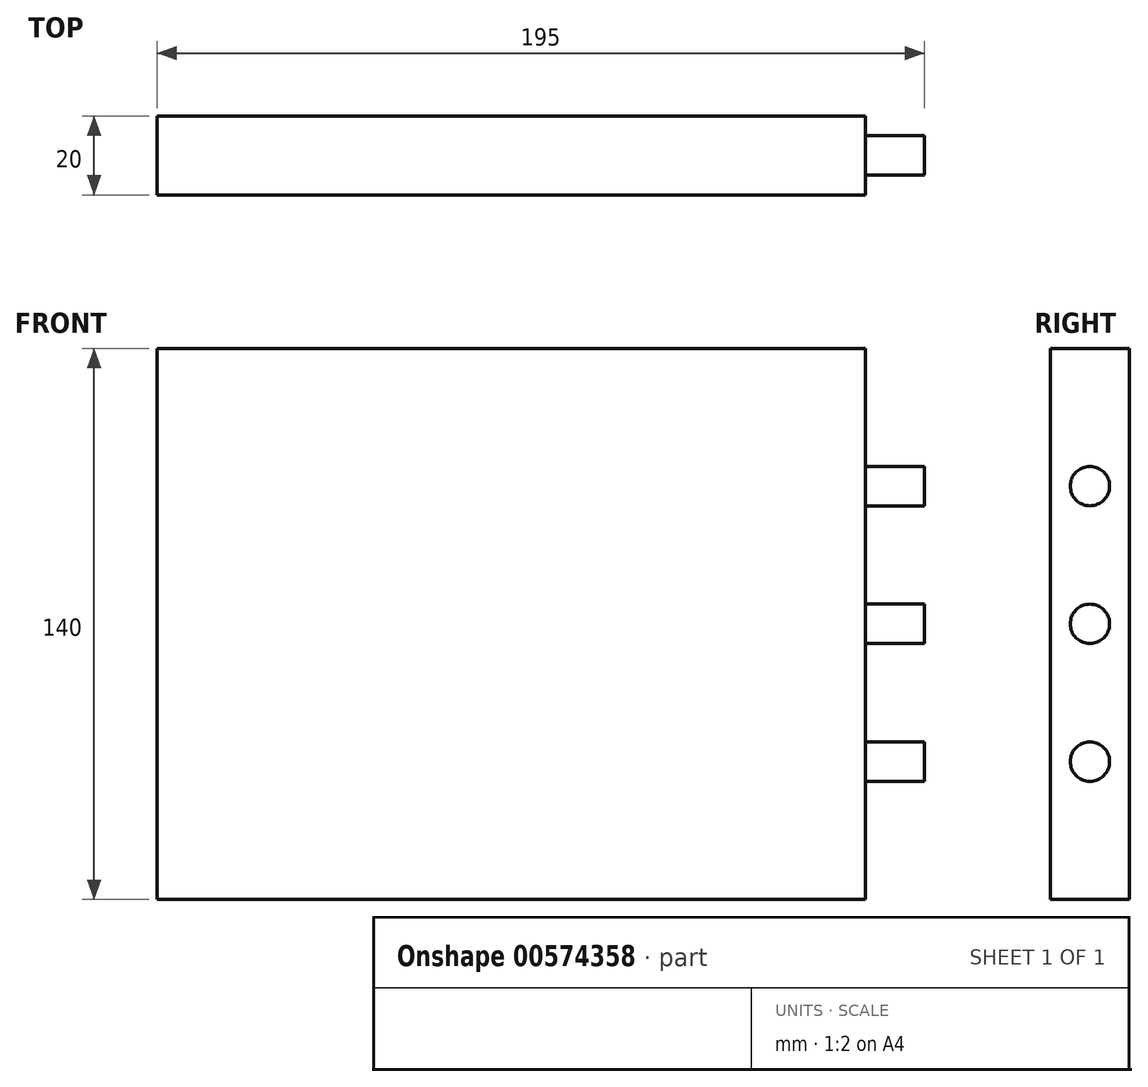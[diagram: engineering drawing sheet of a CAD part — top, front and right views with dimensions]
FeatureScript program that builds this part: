
annotation { "Feature Type Name" : "Feature", "Feature Type Description" : "" }
export const myFeature = defineFeature(function(context is Context, id is Id, definition is map)
    precondition{}
    {
        {
            var Q0;
            Q0=qCreatedBy(makeId("Front.planeOp"),FACE);
            var sketch = newSketch(context, id + "F0", { "sketchPlane" : qUnion([Q0])});
            skLineSegment(sketch, "E0.bottom", {"start": v(-98.8, 76.68) * mm, "end": v(81.2, 76.68) * mm});
            skLineSegment(sketch, "E0.top", {"start": v(-98.8, -63.32) * mm, "end": v(81.2, -63.32) * mm});
            skLineSegment(sketch, "E0.left", {"start": v(-98.8, 76.68) * mm, "end": v(-98.8, -63.32) * mm});
            skLineSegment(sketch, "E0.right", {"start": v(81.2, 76.68) * mm, "end": v(81.2, -63.32) * mm});
            skSolve(sketch);
        }
        {
            var Q0;
            Q0=makeQuery(id+"F0.imprint","IMPRINT",FACE,{"disambiguationData":[TD([[makeQuery(id+"F0.imprint","IMPRINT",EDGE,{"derivedFrom":sQuery(id+"F0.wireOp",EDGE,"E0.bottom")}),-1.0]])]});
            extrude(context, id + "F1", {"entities" : qUnion([Q0]), "depth" : 20 * mm, "offsetDistance" : 25 * mm});
        }
        {
            var Q0;
            Q0=makeQuery(id+"F1.opExtrude","SWEPT_FACE",FACE,{"disambiguationData":[OSD([sQuery(id+"F0.wireOp",EDGE,"E0.right")])]});
            var sketch = newSketch(context, id + "F2", { "sketchPlane" : qUnion([Q0])});
            skCircle(sketch, "E1", {"center": v(-10, 41.68) * mm, "radius": 5 * mm});
            skCircle(sketch, "E2", {"center": v(-10, 6.68) * mm, "radius": 5 * mm});
            skCircle(sketch, "E3", {"center": v(-10, -28.32) * mm, "radius": 5 * mm});
            skSolve(sketch);
        }
        {
            var Q0;
            Q0=makeQuery(id+"F2.imprint","IMPRINT",FACE,{"disambiguationData":[TD([[makeQuery(id+"F2.imprint","IMPRINT",EDGE,{"derivedFrom":sQuery(id+"F2.wireOp",EDGE,"E1")}),1.0]])]});
            var Q1;
            Q1=makeQuery(id+"F2.imprint","IMPRINT",FACE,{"disambiguationData":[TD([[makeQuery(id+"F2.imprint","IMPRINT",EDGE,{"derivedFrom":sQuery(id+"F2.wireOp",EDGE,"E2")}),1.0]])]});
            var Q2;
            Q2=makeQuery(id+"F2.imprint","IMPRINT",FACE,{"disambiguationData":[TD([[makeQuery(id+"F2.imprint","IMPRINT",EDGE,{"derivedFrom":sQuery(id+"F2.wireOp",EDGE,"E3")}),1.0]])]});
            var Q3;
            Q3=sQuery(id+"F2.wireOp",EDGE,"E1");
            var Q4;
            Q4=sQuery(id+"F2.wireOp",EDGE,"E2");
            var Q5;
            Q5=sQuery(id+"F2.wireOp",EDGE,"E3");
            extrude(context, id + "F3", {"entities" : qUnion([Q0, Q1, Q2]), "surfaceEntities" : qUnion([Q3, Q4, Q5]), "depth" : 15 * mm, "offsetDistance" : 25 * mm});
        }
    });
